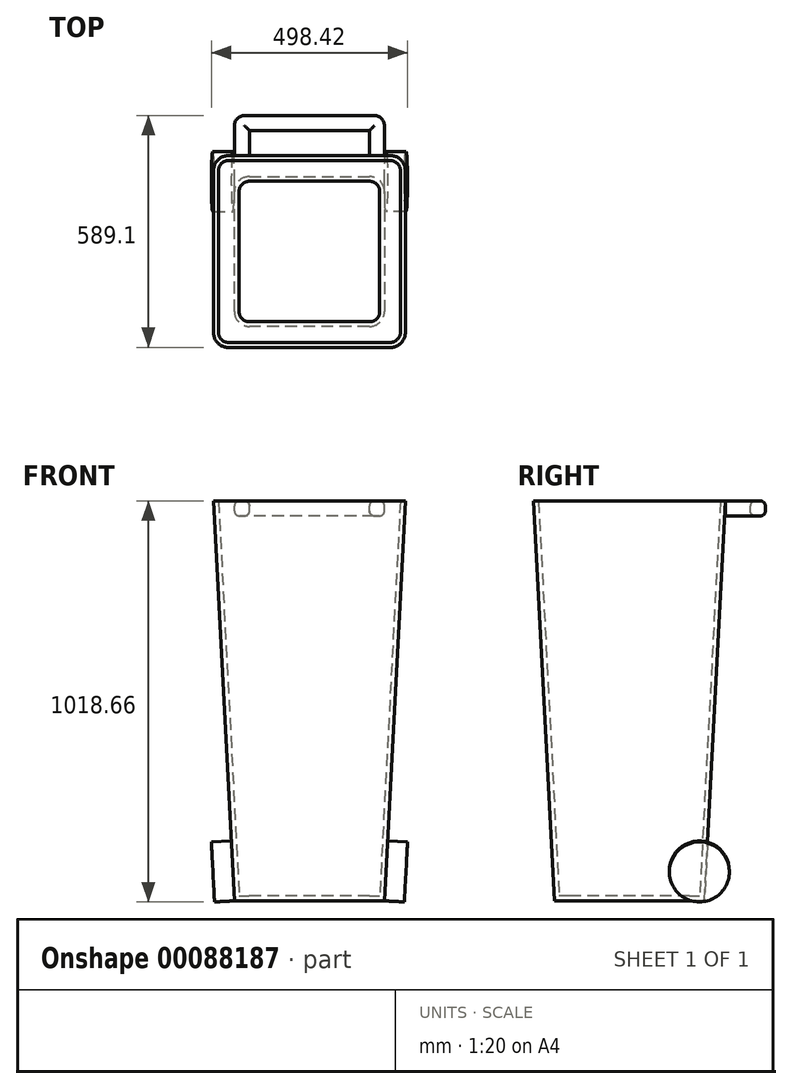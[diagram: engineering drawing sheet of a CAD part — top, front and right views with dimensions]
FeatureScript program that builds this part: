
annotation { "Feature Type Name" : "Feature", "Feature Type Description" : "" }
export const myFeature = defineFeature(function(context is Context, id is Id, definition is map)
    precondition{}
    {
        {
            var Q0;
            Q0=qCreatedBy(makeId("Top.planeOp"),FACE);
            var sketch = newSketch(context, id + "F0", { "sketchPlane" : qUnion([Q0])});
            skLineSegment(sketch, "E0.bottom", {"start": v(190.5, -190.5) * mm, "end": v(-190.5, -190.5) * mm});
            skLineSegment(sketch, "E0.top", {"start": v(190.5, 190.5) * mm, "end": v(-190.5, 190.5) * mm});
            skLineSegment(sketch, "E0.left", {"start": v(190.5, -190.5) * mm, "end": v(190.5, 190.5) * mm});
            skLineSegment(sketch, "E0.right", {"start": v(-190.5, -190.5) * mm, "end": v(-190.5, 190.5) * mm});
            skPoint(sketch, "E0.middle", {"position": v(0, 0) * mm});
            skSolve(sketch);
        }
        {
            var Q0;
            Q0 = qSketchRegion(id + "F0", true);
            extrude(context, id + "F1", {"entities" : qUnion([Q0]), "depth" : 1016 * mm, "hasDraft" : true, "draftAngle" : 3 * degree});
        }
        {
            var Q0;
            Q0=makeQuery(id+"F1.opExtrude","CAP_FACE",FACE,{"disambiguationData":[OSD([sQuery(id+"F0.wireOp",EDGE,"E0.bottom"),sQuery(id+"F0.wireOp",EDGE,"E0.top"),sQuery(id+"F0.wireOp",EDGE,"E0.left"),sQuery(id+"F0.wireOp",EDGE,"E0.right")])],"isStart":false});
            var sketch = newSketch(context, id + "F2", { "sketchPlane" : qUnion([Q0])});
            skLineSegment(sketch, "E1", {"start": v(190.5, 243.75) * mm, "end": v(190.5, 319.95) * mm});
            skLineSegment(sketch, "E2", {"start": v(165.1, 345.35) * mm, "end": v(-165.1, 345.35) * mm});
            skLineSegment(sketch, "E3", {"start": v(-190.5, 319.95) * mm, "end": v(-190.5, 243.75) * mm});
            skLineSegment(sketch, "E4.0", {"start": v(-152.4, 307.25) * mm, "end": v(-152.4, 243.75) * mm});
            skLineSegment(sketch, "E4.1", {"start": v(152.4, 307.25) * mm, "end": v(-152.4, 307.25) * mm});
            skLineSegment(sketch, "E4.2", {"start": v(152.4, 243.75) * mm, "end": v(152.4, 307.25) * mm});
            skLineSegment(sketch, "E5", {"start": v(190.5, 243.75) * mm, "end": v(152.4, 243.75) * mm});
            skLineSegment(sketch, "E6", {"start": v(-152.4, 243.75) * mm, "end": v(-190.5, 243.75) * mm});
            skPoint(sketch, "E7.visualSharp", {"position": v(190.5, 345.35) * mm});
            skArc(sketch, "E7.filletArc", {"start": v(190.5, 319.95) * mm, "mid": v(183.06, 337.9) * mm, "end": v(165.1, 345.35) * mm});
            skPoint(sketch, "E8.visualSharp", {"position": v(-190.5, 345.35) * mm});
            skArc(sketch, "E8.filletArc", {"start": v(-165.1, 345.35) * mm, "mid": v(-183.06, 337.9) * mm, "end": v(-190.5, 319.95) * mm});
            skLineSegment(sketch, "E9", {"start": v(0, 307.25) * mm, "end": v(0, 243.75) * mm, "construction": true});
            skSolve(sketch);
        }
        {
            var Q0;
            Q0 = qSketchRegion(id + "F2", true);
            extrude(context, id + "F3", {"entities" : qUnion([Q0]), "oppositeDirection" : true, "depth" : 38.1 * mm});
        }
        {
            var Q0;
            Q0=makeQuery(id+"F1.opExtrude","SWEPT_FACE",FACE,{"disambiguationData":[OSD([sQuery(id+"F0.wireOp",EDGE,"E0.left")])]});
            var sketch = newSketch(context, id + "F4", { "sketchPlane" : qUnion([Q0])});
            skCircle(sketch, "E10", {"center": v(177.8, 86.17) * mm, "radius": 76.2 * mm});
            skSolve(sketch);
        }
        {
            var Q0;
            Q0 = qSketchRegion(id + "F4", true);
            extrude(context, id + "F5", {"entities" : qUnion([Q0]), "depth" : 50.8 * mm});
        }
        {
            var Q0;
            Q0=makeQuery(id+"F5.opExtrude","SWEPT_BODY",BODY,{"disambiguationData":[OSD([sQuery(id+"F4.wireOp",EDGE,"E10")])]});
            var Q1;
            Q1=qCreatedBy(makeId("Right.planeOp"),FACE);
            mirror(context, id + "F6", {"entities" : qUnion([Q0]), "mirrorPlane" : qUnion([Q1])});
        }
        {
            var Q0;
            Q0=makeQuery(id+"F1.opExtrude","SWEPT_EDGE",EDGE,{"disambiguationData":[OSD([sQuery(id+"F0.wireOp",EDGE,"E0.bottom"),sQuery(id+"F0.wireOp",EDGE,"E0.left")])]});
            var Q1;
            Q1=makeQuery(id+"F1.opExtrude","SWEPT_EDGE",EDGE,{"disambiguationData":[OSD([sQuery(id+"F0.wireOp",EDGE,"E0.top"),sQuery(id+"F0.wireOp",EDGE,"E0.left")])]});
            var Q2;
            Q2=makeQuery(id+"F1.opExtrude","SWEPT_EDGE",EDGE,{"disambiguationData":[OSD([sQuery(id+"F0.wireOp",EDGE,"E0.bottom"),sQuery(id+"F0.wireOp",EDGE,"E0.right")])]});
            var Q3;
            Q3=makeQuery(id+"F1.opExtrude","SWEPT_EDGE",EDGE,{"disambiguationData":[OSD([sQuery(id+"F0.wireOp",EDGE,"E0.top"),sQuery(id+"F0.wireOp",EDGE,"E0.right")])]});
            fillet(context, id + "F7", {"entities" : qUnion([Q0, Q1, Q2, Q3]), "radius" : 38.1 * mm, "tangentPropagation" : true, "allowEdgeOverflow" : false});
        }
        {
            var Q0;
            Q0=makeQuery(id+"F1.opExtrude","CAP_FACE",FACE,{"disambiguationData":[OSD([sQuery(id+"F0.wireOp",EDGE,"E0.bottom"),sQuery(id+"F0.wireOp",EDGE,"E0.top"),sQuery(id+"F0.wireOp",EDGE,"E0.left"),sQuery(id+"F0.wireOp",EDGE,"E0.right")])],"isStart":false});
            shell(context, id + "F8", {"entities" : qUnion([Q0]), "thickness" : 12.7 * mm});
        }
        {
            var Q0;
            Q0=makeQuery(id+"F3.opExtrude","CAP_EDGE",EDGE,{"disambiguationData":[OSD([sQuery(id+"F2.wireOp",EDGE,"E4.2")])],"isStart":true});
            var Q1;
            Q1=makeQuery(id+"F3.opExtrude","CAP_EDGE",EDGE,{"disambiguationData":[OSD([sQuery(id+"F2.wireOp",EDGE,"E4.1")])],"isStart":true});
            var Q2;
            Q2=makeQuery(id+"F3.opExtrude","CAP_EDGE",EDGE,{"disambiguationData":[OSD([sQuery(id+"F2.wireOp",EDGE,"E4.0")])],"isStart":true});
            var Q3;
            Q3=makeQuery(id+"F3.opExtrude","CAP_EDGE",EDGE,{"disambiguationData":[OSD([sQuery(id+"F2.wireOp",EDGE,"E3")])],"isStart":true});
            var Q4;
            Q4=makeQuery(id+"F3.opExtrude","CAP_EDGE",EDGE,{"disambiguationData":[OSD([sQuery(id+"F2.wireOp",EDGE,"E3")])],"isStart":false});
            var Q5;
            Q5=makeQuery(id+"F3.opExtrude","CAP_EDGE",EDGE,{"disambiguationData":[OSD([sQuery(id+"F2.wireOp",EDGE,"E4.0")])],"isStart":false});
            var Q6;
            Q6=makeQuery(id+"F3.opExtrude","CAP_EDGE",EDGE,{"disambiguationData":[OSD([sQuery(id+"F2.wireOp",EDGE,"E4.1")])],"isStart":false});
            var Q7;
            Q7=makeQuery(id+"F3.opExtrude","CAP_EDGE",EDGE,{"disambiguationData":[OSD([sQuery(id+"F2.wireOp",EDGE,"E4.2")])],"isStart":false});
            fillet(context, id + "F9", {"entities" : qUnion([Q0, Q1, Q2, Q3, Q4, Q5, Q6, Q7]), "radius" : 12.7 * mm, "tangentPropagation" : true, "allowEdgeOverflow" : false});
        }
    });
